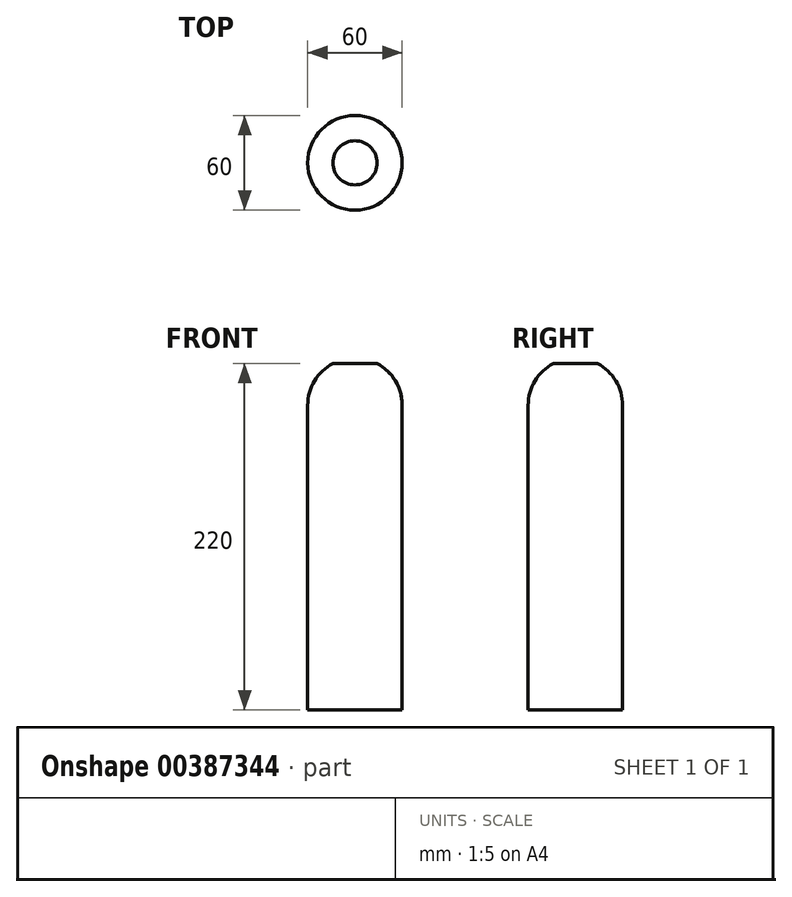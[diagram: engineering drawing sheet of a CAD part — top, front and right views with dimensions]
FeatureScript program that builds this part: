
annotation { "Feature Type Name" : "Feature", "Feature Type Description" : "" }
export const myFeature = defineFeature(function(context is Context, id is Id, definition is map)
    precondition{}
    {
        {
            var Q0;
            Q0=qCreatedBy(makeId("Front.planeOp"),FACE);
            var sketch = newSketch(context, id + "F0", { "sketchPlane" : qUnion([Q0])});
            skLineSegment(sketch, "E0", {"start": v(-30, 0) * mm, "end": v(-30, 193.47) * mm});
            skArc(sketch, "E1", {"start": v(-30, 193.47) * mm, "mid": v(-25.7, 208.96) * mm, "end": v(-14, 220) * mm});
            skLineSegment(sketch, "E2", {"start": v(0, 0) * mm, "end": v(-30, 0) * mm});
            skLineSegment(sketch, "E3", {"start": v(0, 220) * mm, "end": v(0, 0) * mm});
            skLineSegment(sketch, "E4", {"start": v(-14, 220) * mm, "end": v(0, 220) * mm});
            skPoint(sketch, "E5.orphan", {"position": v(0, 223.47) * mm});
            skSolve(sketch);
        }
        {
            var Q0;
            Q0 = qSketchRegion(id + "F0", true);
            var Q1;
            Q1=sQuery(id+"F0.wireOp",EDGE,"E3");
            revolve(context, id + "F1", {"entities" : qUnion([Q0]), "axis" : qUnion([Q1]), "revolveType" : RevolveType.FULL});
        }
    });
